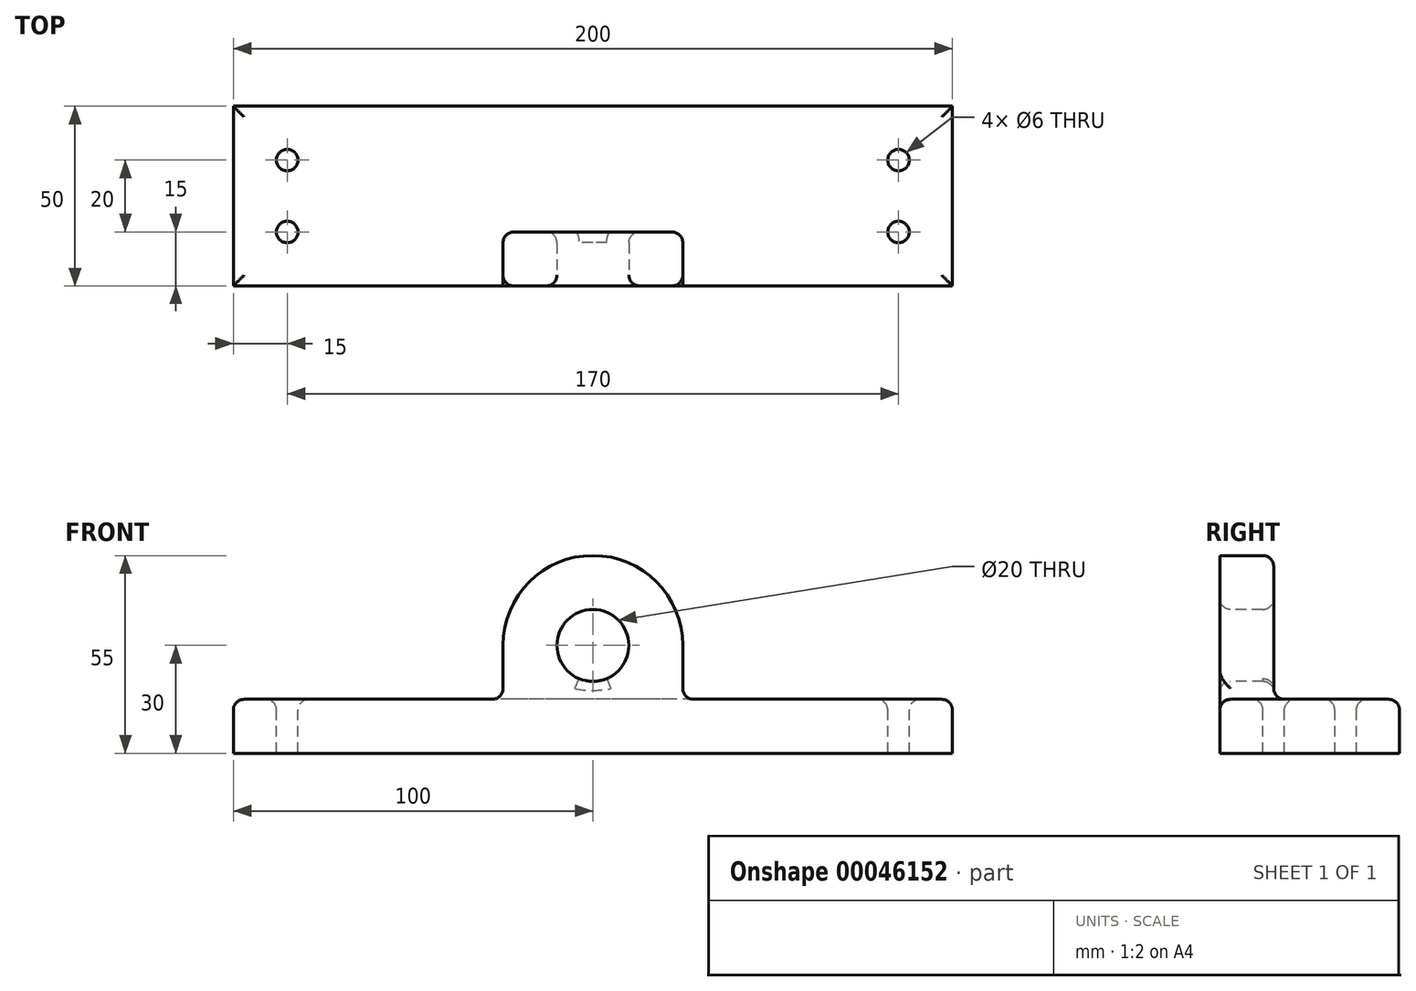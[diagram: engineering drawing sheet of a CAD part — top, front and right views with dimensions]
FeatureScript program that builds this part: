
annotation { "Feature Type Name" : "Feature", "Feature Type Description" : "" }
export const myFeature = defineFeature(function(context is Context, id is Id, definition is map)
    precondition{}
    {
        {
            var Q0;
            Q0=qCreatedBy(makeId("Top.planeOp"),FACE);
            var sketch = newSketch(context, id + "F0", { "sketchPlane" : qUnion([Q0])});
            skLineSegment(sketch, "E0.rect.bottom", {"start": v(100, -25) * mm, "end": v(-100, -25) * mm});
            skLineSegment(sketch, "E0.rect.top", {"start": v(100, 25) * mm, "end": v(-100, 25) * mm});
            skLineSegment(sketch, "E0.rect.left", {"start": v(100, -25) * mm, "end": v(100, 25) * mm});
            skLineSegment(sketch, "E0.rect.right", {"start": v(-100, -25) * mm, "end": v(-100, 25) * mm});
            skPoint(sketch, "E0.rect.middle", {"position": v(0, 0) * mm});
            skSolve(sketch);
        }
        {
            var Q0;
            Q0=makeQuery(id+"F0.imprint","IMPRINT",FACE,{"disambiguationData":[TD([[makeQuery(id+"F0.imprint","IMPRINT",EDGE,{"derivedFrom":sQuery(id+"F0.wireOp",EDGE,"E0.rect.bottom")}),-1.0]])]});
            extrude(context, id + "F1", {"entities" : qUnion([Q0]), "depth" : 15 * mm});
        }
        {
            var Q0;
            Q0=makeQuery(id+"F1.opExtrude","SWEPT_FACE",FACE,{"disambiguationData":[OSD([sQuery(id+"F0.wireOp",EDGE,"E0.rect.bottom")])]});
            var sketch = newSketch(context, id + "F2", { "sketchPlane" : qUnion([Q0])});
            skLineSegment(sketch, "E1", {"start": v(0, 0) * mm, "end": v(0, 30) * mm, "construction": true});
            skCircle(sketch, "E2", {"center": v(0, 30) * mm, "radius": 25 * mm});
            skLineSegment(sketch, "E3.rect.left", {"start": v(-25, 30) * mm, "end": v(-25, 30) * mm});
            skLineSegment(sketch, "E3.rect.right", {"start": v(25, 30) * mm, "end": v(25, 30) * mm});
            skLineSegment(sketch, "E4.bottom", {"start": v(-25, 30) * mm, "end": v(25, 30) * mm});
            skLineSegment(sketch, "E4.top", {"start": v(-25, 0) * mm, "end": v(25, 0) * mm});
            skLineSegment(sketch, "E4.left", {"start": v(-25, 30) * mm, "end": v(-25, 0) * mm});
            skLineSegment(sketch, "E4.right", {"start": v(25, 30) * mm, "end": v(25, 0) * mm});
            skCircle(sketch, "E5", {"center": v(0, 30) * mm, "radius": 10 * mm});
            skSolve(sketch);
        }
        {
            var Q0;
            {var subQ0=sQuery(id+"F2.wireOp",EDGE,"E4.bottom");var subQ1=sQuery(id+"F2.wireOp",EDGE,"E5");var subQ5=makeQuery(id+"F2.imprint","INTERSECT",VERTEX,{"disambiguationData":[OD(0.0)],"derivedFrom":[subQ0,subQ1]});Q0=makeQuery(id+"F2.imprint","IMPRINT",FACE,{"disambiguationData":[TD([[makeQuery(id+"F2.imprint","IMPRINT",EDGE,{"disambiguationData":[TD([[subQ5,1.0]])],"derivedFrom":subQ1}),-1.0]])]});}
            var Q1;
            {var subQ0=sQuery(id+"F2.wireOp",EDGE,"E4.bottom");var subQ1=sQuery(id+"F2.wireOp",EDGE,"E5");var subQ5=makeQuery(id+"F2.imprint","INTERSECT",VERTEX,{"disambiguationData":[OD(0.0)],"derivedFrom":[subQ0,subQ1]});Q1=makeQuery(id+"F2.imprint","IMPRINT",FACE,{"disambiguationData":[TD([[makeQuery(id+"F2.imprint","IMPRINT",EDGE,{"disambiguationData":[TD([[subQ5,-1.0]])],"derivedFrom":subQ1}),-1.0]])]});}
            var Q2;
            {var subQ0=sQuery(id+"F2.wireOp",EDGE,"E4.left");var subQ1=makeQuery(id+"F1.opExtrude","CAP_EDGE",EDGE,{"disambiguationData":[OSD([sQuery(id+"F0.wireOp",EDGE,"E0.rect.bottom")])],"isStart":false});var subQ2=makeQuery(id+"F2.imprint","INTERSECT",VERTEX,{"derivedFrom":[subQ1,subQ0]});Q2=makeQuery(id+"F2.imprint","IMPRINT",FACE,{"disambiguationData":[TD([[makeQuery(id+"F2.imprint","IMPRINT",EDGE,{"disambiguationData":[TD([[subQ2,1.0]])],"derivedFrom":subQ1}),-1.0]])]});}
            var Q3;
            {var subQ0=makeQuery(id+"F1.opExtrude","CAP_EDGE",EDGE,{"disambiguationData":[OSD([sQuery(id+"F0.wireOp",EDGE,"E0.rect.bottom")])],"isStart":false});var subQ3=sQuery(id+"F2.wireOp",EDGE,"E4.right");var subQ4=makeQuery(id+"F2.imprint","INTERSECT",VERTEX,{"derivedFrom":[subQ0,subQ3]});Q3=makeQuery(id+"F2.imprint","IMPRINT",FACE,{"disambiguationData":[TD([[makeQuery(id+"F2.imprint","IMPRINT",EDGE,{"disambiguationData":[TD([[subQ4,-1.0]])],"derivedFrom":subQ0}),-1.0]])]});}
            extrude(context, id + "F3", {"entities" : qUnion([Q0, Q1, Q2, Q3]), "operationType" : NewBodyOperationType.ADD, "oppositeDirection" : true, "depth" : 15 * mm});
        }
        {
            var Q0;
            Q0=makeQuery(id+"F1.opExtrude","CAP_FACE",FACE,{"disambiguationData":[OSD([sQuery(id+"F0.wireOp",EDGE,"E0.rect.bottom"),sQuery(id+"F0.wireOp",EDGE,"E0.rect.top"),sQuery(id+"F0.wireOp",EDGE,"E0.rect.left"),sQuery(id+"F0.wireOp",EDGE,"E0.rect.right")])],"isStart":false});
            var sketch = newSketch(context, id + "F4", { "sketchPlane" : qUnion([Q0])});
            skLineSegment(sketch, "E6.rect.bottom", {"start": v(-85, -10) * mm, "end": v(85, -10) * mm, "construction": true});
            skLineSegment(sketch, "E6.rect.top", {"start": v(-85, 10) * mm, "end": v(85, 10) * mm, "construction": true});
            skLineSegment(sketch, "E6.rect.left", {"start": v(-85, -10) * mm, "end": v(-85, 10) * mm, "construction": true});
            skLineSegment(sketch, "E6.rect.right", {"start": v(85, -10) * mm, "end": v(85, 10) * mm, "construction": true});
            skPoint(sketch, "E6.rect.middle", {"position": v(0, 0) * mm});
            skCircle(sketch, "E7", {"center": v(-85, 10) * mm, "radius": 3 * mm});
            skCircle(sketch, "E8", {"center": v(-85, -10) * mm, "radius": 3 * mm});
            skCircle(sketch, "E9", {"center": v(85, 10) * mm, "radius": 3 * mm});
            skCircle(sketch, "E10", {"center": v(85, -10) * mm, "radius": 3 * mm});
            skSolve(sketch);
        }
        {
            var Q0;
            Q0=makeQuery(id+"F4.imprint","IMPRINT",FACE,{"disambiguationData":[TD([[makeQuery(id+"F4.imprint","IMPRINT",EDGE,{"derivedFrom":sQuery(id+"F4.wireOp",EDGE,"E7")}),1.0]])]});
            var Q1;
            Q1=makeQuery(id+"F4.imprint","IMPRINT",FACE,{"disambiguationData":[TD([[makeQuery(id+"F4.imprint","IMPRINT",EDGE,{"derivedFrom":sQuery(id+"F4.wireOp",EDGE,"E8")}),1.0]])]});
            var Q2;
            Q2=makeQuery(id+"F4.imprint","IMPRINT",FACE,{"disambiguationData":[TD([[makeQuery(id+"F4.imprint","IMPRINT",EDGE,{"derivedFrom":sQuery(id+"F4.wireOp",EDGE,"E9")}),1.0]])]});
            var Q3;
            Q3=makeQuery(id+"F4.imprint","IMPRINT",FACE,{"disambiguationData":[TD([[makeQuery(id+"F4.imprint","IMPRINT",EDGE,{"derivedFrom":sQuery(id+"F4.wireOp",EDGE,"E10")}),1.0]])]});
            extrude(context, id + "F5", {"entities" : qUnion([Q0, Q1, Q2, Q3]), "operationType" : NewBodyOperationType.REMOVE, "oppositeDirection" : true, "depth" : 25 * mm});
        }
        {
            var Q0;
            Q0=makeQuery(id+"F1.opExtrude","CAP_FACE",FACE,{"disambiguationData":[OSD([sQuery(id+"F0.wireOp",EDGE,"E0.rect.bottom"),sQuery(id+"F0.wireOp",EDGE,"E0.rect.top"),sQuery(id+"F0.wireOp",EDGE,"E0.rect.left"),sQuery(id+"F0.wireOp",EDGE,"E0.rect.right")])],"isStart":false});
            var Q1;
            Q1=makeQuery(id+"F3.opExtrude","CAP_EDGE",EDGE,{"disambiguationData":[OSD([sQuery(id+"F2.wireOp",EDGE,"E5")])],"isStart":true});
            var Q2;
            Q2=makeQuery(id+"F3.opExtrude","CAP_EDGE",EDGE,{"disambiguationData":[OSD([sQuery(id+"F2.wireOp",EDGE,"E2")])],"isStart":false});
            var Q3;
            Q3=makeQuery(id+"F3.opExtrude","CAP_EDGE",EDGE,{"disambiguationData":[OSD([sQuery(id+"F2.wireOp",EDGE,"E4.right")])],"isStart":false});
            var Q4;
            Q4=makeQuery(id+"F3.opExtrude","CAP_EDGE",EDGE,{"disambiguationData":[OSD([sQuery(id+"F2.wireOp",EDGE,"E4.left")])],"isStart":false});
            fillet(context, id + "F6", {"entities" : qUnion([Q0, Q1, Q2, Q3, Q4]), "radius" : 3 * mm, "tangentPropagation" : true, "allowEdgeOverflow" : false});
        }
        {
            var Q0;
            Q0=makeQuery(id+"F3.opExtrude","CAP_EDGE",EDGE,{"disambiguationData":[OSD([sQuery(id+"F2.wireOp",EDGE,"E5")])],"isStart":false});
            fillet(context, id + "F7", {"entities" : qUnion([Q0]), "radius" : 3 * mm, "tangentPropagation" : true, "allowEdgeOverflow" : false});
        }
    });
